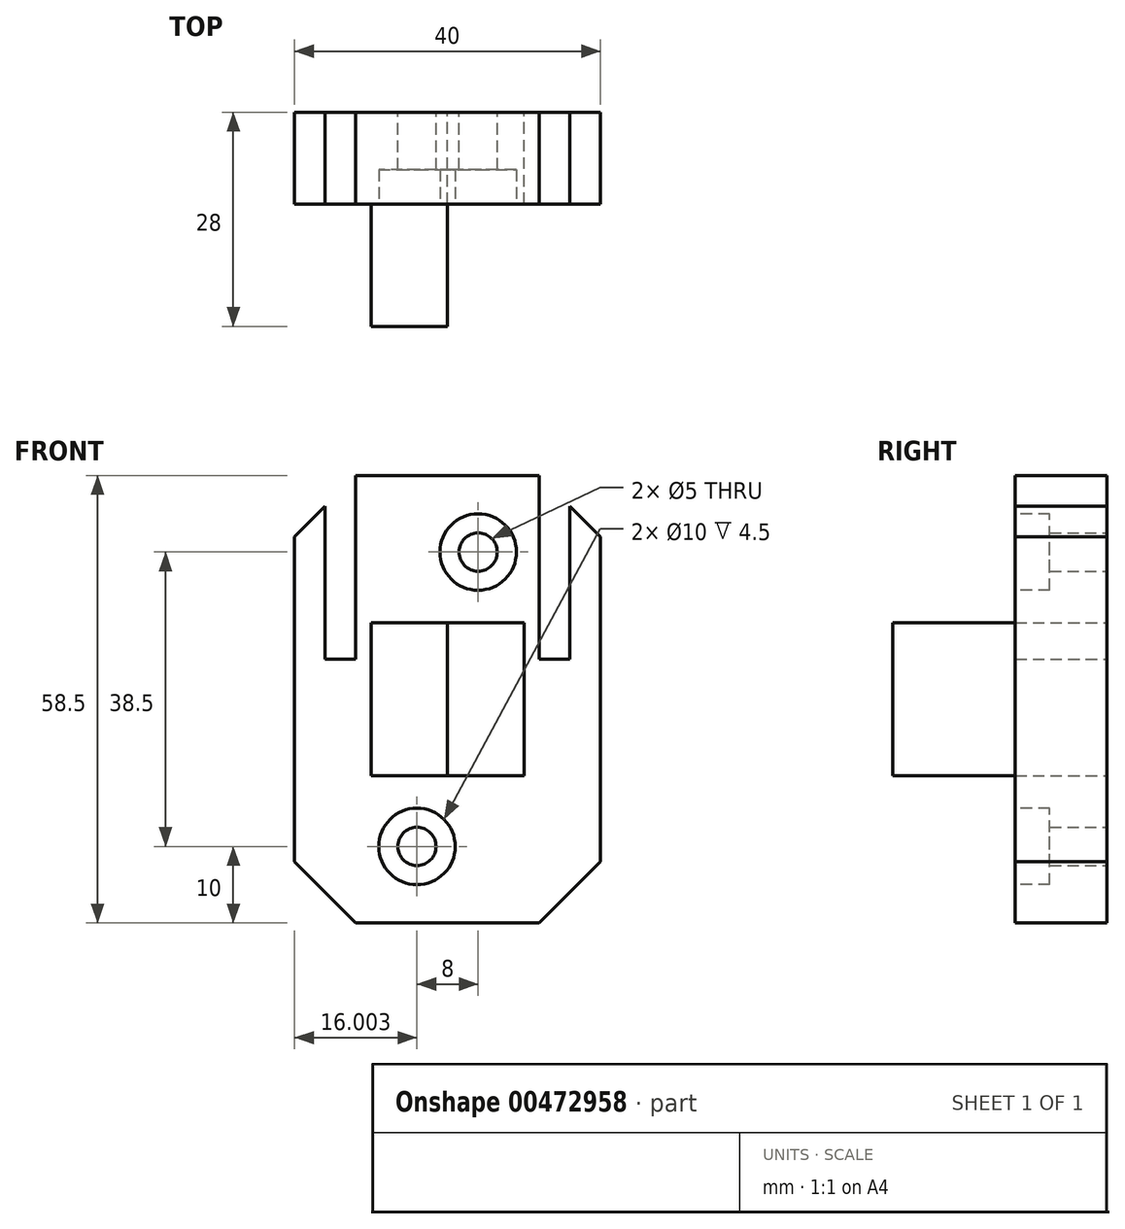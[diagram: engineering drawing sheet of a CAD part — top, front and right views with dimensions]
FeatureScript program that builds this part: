
annotation { "Feature Type Name" : "Feature", "Feature Type Description" : "" }
export const myFeature = defineFeature(function(context is Context, id is Id, definition is map)
    precondition{}
    {
        {
            var Q0;
            Q0=qCreatedBy(makeId("Front.planeOp"),FACE);
            var sketch = newSketch(context, id + "F0", { "sketchPlane" : qUnion([Q0])});
            skLineSegment(sketch, "E0.bottom", {"start": v(10.33, 0) * mm, "end": v(22.33, 0) * mm});
            skLineSegment(sketch, "E0.top", {"start": v(10.33, -58.5) * mm, "end": v(34.33, -58.5) * mm});
            skLineSegment(sketch, "E0.left", {"start": v(2.33, -8) * mm, "end": v(2.33, -50.5) * mm});
            skLineSegment(sketch, "E0.right", {"start": v(42.33, -8) * mm, "end": v(42.33, -50.5) * mm});
            skLineSegment(sketch, "E1", {"start": v(22.33, 0) * mm, "end": v(22.33, -58.5) * mm});
            skLineSegment(sketch, "E2", {"start": v(2.33, -29.25) * mm, "end": v(42.33, -29.25) * mm});
            skCircle(sketch, "E3", {"center": v(18.33, -48.5) * mm, "radius": 2.5 * mm});
            skCircle(sketch, "E4", {"center": v(26.33, -10) * mm, "radius": 2.5 * mm});
            skLineSegment(sketch, "E5", {"start": v(2.33, -8) * mm, "end": v(10.33, 0) * mm});
            skLineSegment(sketch, "E6.MirrorCS", {"start": v(42.33, -8) * mm, "end": v(34.33, 0) * mm});
            skLineSegment(sketch, "E7.MirrorCS", {"start": v(2.33, -50.5) * mm, "end": v(10.33, -58.5) * mm});
            skLineSegment(sketch, "E8.MirrorCS", {"start": v(42.33, -50.5) * mm, "end": v(34.33, -58.5) * mm});
            skPoint(sketch, "E9.orphan", {"position": v(2.33, 0) * mm});
            skPoint(sketch, "E10.orphan", {"position": v(42.33, 0) * mm});
            skPoint(sketch, "E11.orphan", {"position": v(2.33, -58.5) * mm});
            skPoint(sketch, "E12.orphan", {"position": v(42.33, -58.5) * mm});
            skLineSegment(sketch, "E13", {"start": v(22.33, 0) * mm, "end": v(34.33, 0) * mm});
            skLineSegment(sketch, "E14", {"start": v(22.33, -29.25) * mm, "end": v(32.33, -29.25) * mm});
            skLineSegment(sketch, "E15", {"start": v(32.33, -29.25) * mm, "end": v(32.33, -19.25) * mm});
            skLineSegment(sketch, "E16", {"start": v(32.33, -19.25) * mm, "end": v(12.33, -19.25) * mm});
            skLineSegment(sketch, "E17", {"start": v(12.33, -19.25) * mm, "end": v(12.33, -39.25) * mm});
            skLineSegment(sketch, "E18", {"start": v(12.33, -39.25) * mm, "end": v(32.33, -39.25) * mm});
            skLineSegment(sketch, "E19", {"start": v(32.33, -39.25) * mm, "end": v(32.33, -29.25) * mm});
            skSolve(sketch);
        }
        {
            var Q0;
            Q0 = qSketchRegion(id + "F0", true);
            extrude(context, id + "F1", {"entities" : qUnion([Q0]), "depth" : 12 * mm});
        }
        {
            var Q0;
            {var subQ3=sQuery(id+"F0.wireOp",EDGE,"E16");var subQ5=sQuery(id+"F0.wireOp",EDGE,"E17");var subQ7=makeQuery(id+"F0.imprint","INTERSECT",VERTEX,{"derivedFrom":[subQ3,subQ5]});Q0=makeQuery(id+"F0.imprint","IMPRINT",FACE,{"disambiguationData":[TD([[makeQuery(id+"F0.imprint","IMPRINT",EDGE,{"disambiguationData":[TD([[subQ7,1.0]])],"derivedFrom":subQ3}),1.0]])]});}
            var Q1;
            {var subQ0=sQuery(id+"F0.wireOp",EDGE,"E14");Q1=makeQuery(id+"F0.imprint","IMPRINT",FACE,{"disambiguationData":[TD([[makeQuery(id+"F0.imprint","IMPRINT",EDGE,{"derivedFrom":subQ0}),1.0]])]});}
            var Q2;
            {var subQ0=sQuery(id+"F0.wireOp",EDGE,"E14");Q2=makeQuery(id+"F0.imprint","IMPRINT",FACE,{"disambiguationData":[TD([[makeQuery(id+"F0.imprint","IMPRINT",EDGE,{"derivedFrom":subQ0}),-1.0]])]});}
            var Q3;
            {var subQ3=sQuery(id+"F0.wireOp",EDGE,"E18");var subQ5=sQuery(id+"F0.wireOp",EDGE,"E17");var subQ7=makeQuery(id+"F0.imprint","INTERSECT",VERTEX,{"derivedFrom":[subQ5,subQ3]});Q3=makeQuery(id+"F0.imprint","IMPRINT",FACE,{"disambiguationData":[TD([[makeQuery(id+"F0.imprint","IMPRINT",EDGE,{"disambiguationData":[TD([[subQ7,1.0]])],"derivedFrom":subQ5}),1.0]])]});}
            extrude(context, id + "F2", {"entities" : qUnion([Q0, Q1, Q2, Q3]), "operationType" : NewBodyOperationType.ADD, "depth" : 28 * mm});
        }
        {
            var Q0;
            {var subQ0=sQuery(id+"F0.wireOp",EDGE,"E19");var subQ1=sQuery(id+"F0.wireOp",EDGE,"E18");var subQ2=sQuery(id+"F0.wireOp",EDGE,"E17");var subQ3=sQuery(id+"F0.wireOp",EDGE,"E16");var subQ4=sQuery(id+"F0.wireOp",EDGE,"E15");Q0=makeQuery(id+"F2.boolean.opBoolean","MERGE",FACE,{"derivedFrom":[makeQuery(id+"F1.opExtrude","CAP_FACE",FACE,{"disambiguationData":[OSD([sQuery(id+"F0.wireOp",EDGE,"E0.bottom"),sQuery(id+"F0.wireOp",EDGE,"E0.top"),sQuery(id+"F0.wireOp",EDGE,"E0.left"),sQuery(id+"F0.wireOp",EDGE,"E0.right"),sQuery(id+"F0.wireOp",EDGE,"E3"),sQuery(id+"F0.wireOp",EDGE,"E4"),sQuery(id+"F0.wireOp",EDGE,"E5"),sQuery(id+"F0.wireOp",EDGE,"E6.MirrorCS"),sQuery(id+"F0.wireOp",EDGE,"E7.MirrorCS"),sQuery(id+"F0.wireOp",EDGE,"E8.MirrorCS"),sQuery(id+"F0.wireOp",EDGE,"E13"),subQ4,subQ3,subQ2,subQ1,subQ0])],"isStart":true}),makeQuery(id+"F2.opExtrude","CAP_FACE",FACE,{"disambiguationData":[OSD([subQ4,subQ3,subQ2,subQ1,subQ0])],"isStart":true})]});}
            var sketch = newSketch(context, id + "F3", { "sketchPlane" : qUnion([Q0])});
            skLineSegment(sketch, "E20", {"start": v(-42.33, -8) * mm, "end": v(-34.33, -8) * mm});
            skLineSegment(sketch, "E21", {"start": v(-34.33, -8) * mm, "end": v(-34.33, 0) * mm});
            skSolve(sketch);
        }
        {
            var Q0;
            Q0=makeQuery(id+"F3.imprint","IMPRINT",FACE,{"disambiguationData":[TD([[makeQuery(id+"F3.imprint","IMPRINT",EDGE,{"derivedFrom":sQuery(id+"F3.wireOp",EDGE,"E20")}),1.0]])]});
            extrude(context, id + "F4", {"entities" : qUnion([Q0]), "operationType" : NewBodyOperationType.REMOVE, "oppositeDirection" : true, "depth" : 25 * mm});
        }
        {
            var Q0;
            Q0=makeQuery(id+"F4.boolean.opBoolean","COPY",FACE,{"derivedFrom":makeQuery(id+"F4.opExtrude","SWEPT_FACE",FACE,{"disambiguationData":[OSD([sQuery(id+"F3.wireOp",EDGE,"E20")])]})});
            var sketch = newSketch(context, id + "F5", { "sketchPlane" : qUnion([Q0])});
            skLineSegment(sketch, "E22", {"start": v(42.33, -6) * mm, "end": v(34.33, -6) * mm});
            skLineSegment(sketch, "E23", {"start": v(38.33, -12) * mm, "end": v(38.33, 0) * mm});
            skCircle(sketch, "E24", {"center": v(38.33, -6) * mm, "radius": 1.5 * mm});
            skSolve(sketch);
        }
        {
            var Q0;
            {var subQ0=sQuery(id+"F5.wireOp",EDGE,"E23");var subQ1=sQuery(id+"F5.wireOp",EDGE,"E22");var subQ2=makeQuery(id+"F5.imprint","INTERSECT",VERTEX,{"derivedFrom":[subQ1,subQ0]});Q0=makeQuery(id+"F5.imprint","IMPRINT",FACE,{"disambiguationData":[TD([[makeQuery(id+"F5.imprint","IMPRINT",EDGE,{"disambiguationData":[TD([[subQ2,-1.0]])],"derivedFrom":subQ1}),-1.0]])]});}
            var Q1;
            {var subQ0=sQuery(id+"F5.wireOp",EDGE,"E23");var subQ1=sQuery(id+"F5.wireOp",EDGE,"E22");var subQ2=makeQuery(id+"F5.imprint","INTERSECT",VERTEX,{"derivedFrom":[subQ1,subQ0]});Q1=makeQuery(id+"F5.imprint","IMPRINT",FACE,{"disambiguationData":[TD([[makeQuery(id+"F5.imprint","IMPRINT",EDGE,{"disambiguationData":[TD([[subQ2,-1.0]])],"derivedFrom":subQ1}),1.0]])]});}
            var Q2;
            {var subQ0=sQuery(id+"F5.wireOp",EDGE,"E24");var subQ1=sQuery(id+"F5.wireOp",EDGE,"E22");var subQ2=makeQuery(id+"F5.imprint","INTERSECT",VERTEX,{"disambiguationData":[OD(0.0)],"derivedFrom":[subQ1,subQ0]});Q2=makeQuery(id+"F5.imprint","IMPRINT",FACE,{"disambiguationData":[TD([[makeQuery(id+"F5.imprint","IMPRINT",EDGE,{"disambiguationData":[TD([[subQ2,-1.0]])],"derivedFrom":subQ1}),1.0]])]});}
            var Q3;
            {var subQ0=sQuery(id+"F5.wireOp",EDGE,"E24");var subQ1=sQuery(id+"F5.wireOp",EDGE,"E22");var subQ2=makeQuery(id+"F5.imprint","INTERSECT",VERTEX,{"disambiguationData":[OD(0.0)],"derivedFrom":[subQ1,subQ0]});Q3=makeQuery(id+"F5.imprint","IMPRINT",FACE,{"disambiguationData":[TD([[makeQuery(id+"F5.imprint","IMPRINT",EDGE,{"disambiguationData":[TD([[subQ2,-1.0]])],"derivedFrom":subQ1}),-1.0]])]});}
            extrude(context, id + "F6", {"entities" : qUnion([Q0, Q1, Q2, Q3]), "operationType" : NewBodyOperationType.REMOVE, "oppositeDirection" : true, "depth" : 16 * mm});
        }
        {
            var Q0;
            {var subQ0=sQuery(id+"F0.wireOp",EDGE,"E19");var subQ1=sQuery(id+"F0.wireOp",EDGE,"E18");var subQ2=sQuery(id+"F0.wireOp",EDGE,"E17");var subQ3=sQuery(id+"F0.wireOp",EDGE,"E16");var subQ4=sQuery(id+"F0.wireOp",EDGE,"E15");Q0=makeQuery(id+"F2.boolean.opBoolean","MERGE",FACE,{"derivedFrom":[makeQuery(id+"F1.opExtrude","CAP_FACE",FACE,{"disambiguationData":[OSD([sQuery(id+"F0.wireOp",EDGE,"E0.bottom"),sQuery(id+"F0.wireOp",EDGE,"E0.top"),sQuery(id+"F0.wireOp",EDGE,"E0.left"),sQuery(id+"F0.wireOp",EDGE,"E0.right"),sQuery(id+"F0.wireOp",EDGE,"E3"),sQuery(id+"F0.wireOp",EDGE,"E4"),sQuery(id+"F0.wireOp",EDGE,"E5"),sQuery(id+"F0.wireOp",EDGE,"E6.MirrorCS"),sQuery(id+"F0.wireOp",EDGE,"E7.MirrorCS"),sQuery(id+"F0.wireOp",EDGE,"E8.MirrorCS"),sQuery(id+"F0.wireOp",EDGE,"E13"),subQ4,subQ3,subQ2,subQ1,subQ0])],"isStart":true}),makeQuery(id+"F2.opExtrude","CAP_FACE",FACE,{"disambiguationData":[OSD([subQ4,subQ3,subQ2,subQ1,subQ0])],"isStart":true})]});}
            var sketch = newSketch(context, id + "F7", { "sketchPlane" : qUnion([Q0])});
            skLineSegment(sketch, "E25", {"start": v(-38.33, -8) * mm, "end": v(-38.33, 0) * mm});
            skLineSegment(sketch, "E26", {"start": v(-22.33, 0) * mm, "end": v(-22.33, -14.44) * mm});
            skPoint(sketch, "E26.endSnap0", {"position": v(-22.33, 0) * mm});
            skLineSegment(sketch, "E27.MirrorCS", {"start": v(-6.33, -8) * mm, "end": v(-6.33, 0) * mm});
            skLineSegment(sketch, "E28", {"start": v(-2.33, -8) * mm, "end": v(-10.33, -8) * mm});
            skLineSegment(sketch, "E29", {"start": v(-10.33, -8) * mm, "end": v(-10.33, 0) * mm});
            skSolve(sketch);
        }
        {
            var Q0;
            {var subQ5=sQuery(id+"F7.wireOp",EDGE,"E29");Q0=makeQuery(id+"F7.imprint","IMPRINT",FACE,{"disambiguationData":[TD([[makeQuery(id+"F7.imprint","IMPRINT",EDGE,{"derivedFrom":subQ5}),-1.0]])]});}
            var Q1;
            {var subQ0=sQuery(id+"F7.wireOp",EDGE,"E28");var subQ1=sQuery(id+"F7.wireOp",EDGE,"E27.MirrorCS");var subQ2=makeQuery(id+"F7.imprint","INTERSECT",VERTEX,{"derivedFrom":[subQ1,subQ0]});Q1=makeQuery(id+"F7.imprint","IMPRINT",FACE,{"disambiguationData":[TD([[makeQuery(id+"F7.imprint","IMPRINT",EDGE,{"disambiguationData":[TD([[subQ2,-1.0]])],"derivedFrom":subQ1}),-1.0]])]});}
            extrude(context, id + "F8", {"entities" : qUnion([Q0, Q1]), "operationType" : NewBodyOperationType.REMOVE, "oppositeDirection" : true, "depth" : 25 * mm});
        }
        {
            var Q0;
            Q0=makeQuery(id+"F8.boolean.opBoolean","COPY",FACE,{"derivedFrom":makeQuery(id+"F8.opExtrude","SWEPT_FACE",FACE,{"disambiguationData":[OSD([sQuery(id+"F7.wireOp",EDGE,"E28")])]})});
            var sketch = newSketch(context, id + "F9", { "sketchPlane" : qUnion([Q0])});
            skLineSegment(sketch, "E30", {"start": v(2.33, -6) * mm, "end": v(10.33, -6) * mm});
            skLineSegment(sketch, "E31", {"start": v(6.33, -12) * mm, "end": v(6.33, 0) * mm});
            skCircle(sketch, "E32", {"center": v(6.33, -6) * mm, "radius": 1.5 * mm});
            skSolve(sketch);
        }
        {
            var Q0;
            {var subQ0=sQuery(id+"F9.wireOp",EDGE,"E32");var subQ1=sQuery(id+"F9.wireOp",EDGE,"E30");var subQ2=makeQuery(id+"F9.imprint","INTERSECT",VERTEX,{"disambiguationData":[OD(0.0)],"derivedFrom":[subQ1,subQ0]});Q0=makeQuery(id+"F9.imprint","IMPRINT",FACE,{"disambiguationData":[TD([[makeQuery(id+"F9.imprint","IMPRINT",EDGE,{"disambiguationData":[TD([[subQ2,-1.0]])],"derivedFrom":subQ1}),-1.0]])]});}
            var Q1;
            {var subQ0=sQuery(id+"F9.wireOp",EDGE,"E32");var subQ1=sQuery(id+"F9.wireOp",EDGE,"E30");var subQ2=makeQuery(id+"F9.imprint","INTERSECT",VERTEX,{"disambiguationData":[OD(0.0)],"derivedFrom":[subQ1,subQ0]});Q1=makeQuery(id+"F9.imprint","IMPRINT",FACE,{"disambiguationData":[TD([[makeQuery(id+"F9.imprint","IMPRINT",EDGE,{"disambiguationData":[TD([[subQ2,-1.0]])],"derivedFrom":subQ1}),1.0]])]});}
            var Q2;
            {var subQ0=sQuery(id+"F9.wireOp",EDGE,"E31");var subQ1=sQuery(id+"F9.wireOp",EDGE,"E30");var subQ2=makeQuery(id+"F9.imprint","INTERSECT",VERTEX,{"derivedFrom":[subQ1,subQ0]});Q2=makeQuery(id+"F9.imprint","IMPRINT",FACE,{"disambiguationData":[TD([[makeQuery(id+"F9.imprint","IMPRINT",EDGE,{"disambiguationData":[TD([[subQ2,-1.0]])],"derivedFrom":subQ1}),1.0]])]});}
            var Q3;
            {var subQ0=sQuery(id+"F9.wireOp",EDGE,"E31");var subQ1=sQuery(id+"F9.wireOp",EDGE,"E30");var subQ2=makeQuery(id+"F9.imprint","INTERSECT",VERTEX,{"derivedFrom":[subQ1,subQ0]});Q3=makeQuery(id+"F9.imprint","IMPRINT",FACE,{"disambiguationData":[TD([[makeQuery(id+"F9.imprint","IMPRINT",EDGE,{"disambiguationData":[TD([[subQ2,-1.0]])],"derivedFrom":subQ1}),-1.0]])]});}
            extrude(context, id + "F10", {"entities" : qUnion([Q0, Q1, Q2, Q3]), "operationType" : NewBodyOperationType.REMOVE, "oppositeDirection" : true, "depth" : 16 * mm});
        }
        {
            var Q0;
            Q0=makeQuery(id+"F8.boolean.opBoolean","COPY",FACE,{"derivedFrom":makeQuery(id+"F8.opExtrude","SWEPT_FACE",FACE,{"disambiguationData":[OSD([sQuery(id+"F7.wireOp",EDGE,"E28")])]})});
            extrude(context, id + "F11", {"entities" : qUnion([Q0]), "operationType" : NewBodyOperationType.ADD, "depth" : 25 * mm});
        }
        {
            var Q0;
            {var subQ0=sQuery(id+"F0.wireOp",EDGE,"E19");var subQ1=sQuery(id+"F0.wireOp",EDGE,"E18");var subQ2=sQuery(id+"F0.wireOp",EDGE,"E17");var subQ3=sQuery(id+"F0.wireOp",EDGE,"E16");var subQ4=sQuery(id+"F0.wireOp",EDGE,"E15");var subQ5=sQuery(id+"F0.wireOp",EDGE,"E13");var subQ6=sQuery(id+"F0.wireOp",EDGE,"E8.MirrorCS");var subQ7=sQuery(id+"F0.wireOp",EDGE,"E7.MirrorCS");var subQ8=sQuery(id+"F0.wireOp",EDGE,"E6.MirrorCS");var subQ9=sQuery(id+"F0.wireOp",EDGE,"E5");var subQ10=sQuery(id+"F0.wireOp",EDGE,"E4");var subQ11=sQuery(id+"F0.wireOp",EDGE,"E3");var subQ12=sQuery(id+"F0.wireOp",EDGE,"E0.right");var subQ13=sQuery(id+"F0.wireOp",EDGE,"E0.left");var subQ14=sQuery(id+"F0.wireOp",EDGE,"E0.top");var subQ15=sQuery(id+"F0.wireOp",EDGE,"E0.bottom");Q0=makeQuery(id+"F11.boolean.opBoolean","MERGE",FACE,{"derivedFrom":[makeQuery(id+"F1.opExtrude","CAP_FACE",FACE,{"disambiguationData":[OSD([subQ15,subQ14,subQ13,subQ12,subQ11,subQ10,subQ9,subQ8,subQ7,subQ6,subQ5,subQ4,subQ3,subQ2,subQ1,subQ0])],"isStart":false}),makeQuery(id+"F11.opExtrude","SWEPT_FACE",FACE,{"disambiguationData":[OSD([subQ15,subQ14,subQ13,subQ12,subQ11,subQ10,subQ9,subQ8,subQ7,subQ6,subQ5,subQ4,subQ3,subQ2,subQ1,subQ0,sQuery(id+"F7.wireOp",EDGE,"E28")])]})]});}
            var sketch = newSketch(context, id + "F12", { "sketchPlane" : qUnion([Q0])});
            skLineSegment(sketch, "E33", {"start": v(10.33, 0) * mm, "end": v(10.33, -8) * mm});
            skLineSegment(sketch, "E34", {"start": v(10.33, -8) * mm, "end": v(2.33, -8) * mm});
            skLineSegment(sketch, "E35", {"start": v(2.33, -8) * mm, "end": v(10.33, 0) * mm});
            skSolve(sketch);
        }
        {
            var Q0;
            {var subQ0=sQuery(id+"F12.wireOp",EDGE,"E35");Q0=makeQuery(id+"F12.imprint","IMPRINT",FACE,{"disambiguationData":[TD([[makeQuery(id+"F12.imprint","IMPRINT",EDGE,{"derivedFrom":subQ0}),1.0]])]});}
            extrude(context, id + "F13", {"entities" : qUnion([Q0]), "operationType" : NewBodyOperationType.REMOVE, "oppositeDirection" : true, "depth" : 25 * mm});
        }
        {
            var Q0;
            Q0=makeQuery(id+"F4.boolean.opBoolean","COPY",FACE,{"derivedFrom":makeQuery(id+"F4.opExtrude","SWEPT_FACE",FACE,{"disambiguationData":[OSD([sQuery(id+"F3.wireOp",EDGE,"E20")])]})});
            extrude(context, id + "F14", {"entities" : qUnion([Q0]), "operationType" : NewBodyOperationType.ADD, "depth" : 25 * mm});
        }
        {
            var Q0;
            {var subQ0=sQuery(id+"F0.wireOp",EDGE,"E19");var subQ1=sQuery(id+"F0.wireOp",EDGE,"E18");var subQ2=sQuery(id+"F0.wireOp",EDGE,"E17");var subQ3=sQuery(id+"F0.wireOp",EDGE,"E16");var subQ4=sQuery(id+"F0.wireOp",EDGE,"E15");var subQ5=sQuery(id+"F0.wireOp",EDGE,"E13");var subQ6=sQuery(id+"F0.wireOp",EDGE,"E8.MirrorCS");var subQ7=sQuery(id+"F0.wireOp",EDGE,"E7.MirrorCS");var subQ8=sQuery(id+"F0.wireOp",EDGE,"E6.MirrorCS");var subQ9=sQuery(id+"F0.wireOp",EDGE,"E5");var subQ10=sQuery(id+"F0.wireOp",EDGE,"E4");var subQ11=sQuery(id+"F0.wireOp",EDGE,"E3");var subQ12=sQuery(id+"F0.wireOp",EDGE,"E0.right");var subQ13=sQuery(id+"F0.wireOp",EDGE,"E0.left");var subQ14=sQuery(id+"F0.wireOp",EDGE,"E0.top");var subQ15=sQuery(id+"F0.wireOp",EDGE,"E0.bottom");Q0=makeQuery(id+"F14.boolean.opBoolean","MERGE",FACE,{"derivedFrom":[makeQuery(id+"F11.boolean.opBoolean","MERGE",FACE,{"derivedFrom":[makeQuery(id+"F1.opExtrude","CAP_FACE",FACE,{"disambiguationData":[OSD([subQ15,subQ14,subQ13,subQ12,subQ11,subQ10,subQ9,subQ8,subQ7,subQ6,subQ5,subQ4,subQ3,subQ2,subQ1,subQ0])],"isStart":false}),makeQuery(id+"F11.opExtrude","SWEPT_FACE",FACE,{"disambiguationData":[OSD([subQ15,subQ14,subQ13,subQ12,subQ11,subQ10,subQ9,subQ8,subQ7,subQ6,subQ5,subQ4,subQ3,subQ2,subQ1,subQ0,sQuery(id+"F7.wireOp",EDGE,"E28")])]})]}),makeQuery(id+"F14.opExtrude","SWEPT_FACE",FACE,{"disambiguationData":[OSD([subQ15,subQ14,subQ13,subQ12,subQ11,subQ10,subQ9,subQ8,subQ7,subQ6,subQ5,subQ4,subQ3,subQ2,subQ1,subQ0,sQuery(id+"F3.wireOp",EDGE,"E20")])]})]});}
            var sketch = newSketch(context, id + "F15", { "sketchPlane" : qUnion([Q0])});
            skLineSegment(sketch, "E36", {"start": v(34.33, 0) * mm, "end": v(34.33, -8) * mm});
            skLineSegment(sketch, "E37", {"start": v(34.33, -8) * mm, "end": v(42.33, -8) * mm});
            skLineSegment(sketch, "E38", {"start": v(42.33, -8) * mm, "end": v(34.33, 0) * mm});
            skSolve(sketch);
        }
        {
            var Q0;
            {var subQ0=sQuery(id+"F15.wireOp",EDGE,"E38");Q0=makeQuery(id+"F15.imprint","IMPRINT",FACE,{"disambiguationData":[TD([[makeQuery(id+"F15.imprint","IMPRINT",EDGE,{"derivedFrom":subQ0}),-1.0]])]});}
            extrude(context, id + "F16", {"entities" : qUnion([Q0]), "operationType" : NewBodyOperationType.REMOVE, "oppositeDirection" : true, "depth" : 25 * mm});
        }
        {
            var Q0;
            Q0=makeQuery(id+"F2.opExtrude","SWEPT_FACE",FACE,{"disambiguationData":[OSD([sQuery(id+"F0.wireOp",EDGE,"E16")])]});
            var sketch = newSketch(context, id + "F17", { "sketchPlane" : qUnion([Q0])});
            skLineSegment(sketch, "E39", {"start": v(12.33, -20) * mm, "end": v(32.33, -20) * mm});
            skLineSegment(sketch, "E40", {"start": v(22.33, -12) * mm, "end": v(22.33, -28) * mm});
            skCircle(sketch, "E41", {"center": v(22.33, -20) * mm, "radius": 4 * mm});
            skSolve(sketch);
        }
        {
            var Q0;
            {var subQ0=sQuery(id+"F17.wireOp",EDGE,"E41");var subQ1=sQuery(id+"F17.wireOp",EDGE,"E39");var subQ2=makeQuery(id+"F17.imprint","INTERSECT",VERTEX,{"disambiguationData":[OD(0.0)],"derivedFrom":[subQ1,subQ0]});Q0=makeQuery(id+"F17.imprint","IMPRINT",FACE,{"disambiguationData":[TD([[makeQuery(id+"F17.imprint","IMPRINT",EDGE,{"disambiguationData":[TD([[subQ2,-1.0]])],"derivedFrom":subQ1}),-1.0]])]});}
            var Q1;
            {var subQ0=sQuery(id+"F17.wireOp",EDGE,"E41");var subQ1=sQuery(id+"F17.wireOp",EDGE,"E39");var subQ2=makeQuery(id+"F17.imprint","INTERSECT",VERTEX,{"disambiguationData":[OD(0.0)],"derivedFrom":[subQ1,subQ0]});Q1=makeQuery(id+"F17.imprint","IMPRINT",FACE,{"disambiguationData":[TD([[makeQuery(id+"F17.imprint","IMPRINT",EDGE,{"disambiguationData":[TD([[subQ2,-1.0]])],"derivedFrom":subQ1}),1.0]])]});}
            var Q2;
            {var subQ0=sQuery(id+"F17.wireOp",EDGE,"E40");var subQ1=sQuery(id+"F17.wireOp",EDGE,"E39");var subQ2=makeQuery(id+"F17.imprint","INTERSECT",VERTEX,{"derivedFrom":[subQ1,subQ0]});Q2=makeQuery(id+"F17.imprint","IMPRINT",FACE,{"disambiguationData":[TD([[makeQuery(id+"F17.imprint","IMPRINT",EDGE,{"disambiguationData":[TD([[subQ2,-1.0]])],"derivedFrom":subQ1}),1.0]])]});}
            var Q3;
            {var subQ0=sQuery(id+"F17.wireOp",EDGE,"E40");var subQ1=sQuery(id+"F17.wireOp",EDGE,"E39");var subQ2=makeQuery(id+"F17.imprint","INTERSECT",VERTEX,{"derivedFrom":[subQ1,subQ0]});Q3=makeQuery(id+"F17.imprint","IMPRINT",FACE,{"disambiguationData":[TD([[makeQuery(id+"F17.imprint","IMPRINT",EDGE,{"disambiguationData":[TD([[subQ2,-1.0]])],"derivedFrom":subQ1}),-1.0]])]});}
            extrude(context, id + "F18", {"entities" : qUnion([Q0, Q1, Q2, Q3]), "operationType" : NewBodyOperationType.REMOVE, "oppositeDirection" : true, "depth" : 25 * mm});
        }
        {
            var Q0;
            {var subQ0=sQuery(id+"F0.wireOp",EDGE,"E19");var subQ1=sQuery(id+"F0.wireOp",EDGE,"E18");var subQ2=sQuery(id+"F0.wireOp",EDGE,"E17");var subQ3=sQuery(id+"F0.wireOp",EDGE,"E16");var subQ4=sQuery(id+"F0.wireOp",EDGE,"E15");var subQ5=sQuery(id+"F0.wireOp",EDGE,"E13");var subQ6=sQuery(id+"F0.wireOp",EDGE,"E8.MirrorCS");var subQ7=sQuery(id+"F0.wireOp",EDGE,"E7.MirrorCS");var subQ8=sQuery(id+"F0.wireOp",EDGE,"E6.MirrorCS");var subQ9=sQuery(id+"F0.wireOp",EDGE,"E5");var subQ10=sQuery(id+"F0.wireOp",EDGE,"E4");var subQ11=sQuery(id+"F0.wireOp",EDGE,"E3");var subQ12=sQuery(id+"F0.wireOp",EDGE,"E0.right");var subQ13=sQuery(id+"F0.wireOp",EDGE,"E0.left");var subQ14=sQuery(id+"F0.wireOp",EDGE,"E0.top");var subQ15=sQuery(id+"F0.wireOp",EDGE,"E0.bottom");Q0=makeQuery(id+"F14.boolean.opBoolean","MERGE",FACE,{"derivedFrom":[makeQuery(id+"F11.boolean.opBoolean","MERGE",FACE,{"derivedFrom":[makeQuery(id+"F1.opExtrude","CAP_FACE",FACE,{"disambiguationData":[OSD([subQ15,subQ14,subQ13,subQ12,subQ11,subQ10,subQ9,subQ8,subQ7,subQ6,subQ5,subQ4,subQ3,subQ2,subQ1,subQ0])],"isStart":false}),makeQuery(id+"F11.opExtrude","SWEPT_FACE",FACE,{"disambiguationData":[OSD([subQ15,subQ14,subQ13,subQ12,subQ11,subQ10,subQ9,subQ8,subQ7,subQ6,subQ5,subQ4,subQ3,subQ2,subQ1,subQ0,sQuery(id+"F7.wireOp",EDGE,"E28")])]})]}),makeQuery(id+"F14.opExtrude","SWEPT_FACE",FACE,{"disambiguationData":[OSD([subQ15,subQ14,subQ13,subQ12,subQ11,subQ10,subQ9,subQ8,subQ7,subQ6,subQ5,subQ4,subQ3,subQ2,subQ1,subQ0,sQuery(id+"F3.wireOp",EDGE,"E20")])]})]});}
            var sketch = newSketch(context, id + "F19", { "sketchPlane" : qUnion([Q0])});
            skCircle(sketch, "E42", {"center": v(26.33, -10) * mm, "radius": 5 * mm});
            skCircle(sketch, "E43", {"center": v(18.33, -48.5) * mm, "radius": 5 * mm});
            skSolve(sketch);
        }
        {
            var Q0;
            Q0=makeQuery(id+"F19.imprint","IMPRINT",FACE,{"disambiguationData":[TD([[makeQuery(id+"F19.imprint","IMPRINT",EDGE,{"derivedFrom":sQuery(id+"F19.wireOp",EDGE,"E42")}),1.0]])]});
            extrude(context, id + "F20", {"entities" : qUnion([Q0]), "operationType" : NewBodyOperationType.REMOVE, "oppositeDirection" : true, "depth" : 4.5 * mm});
        }
        {
            var Q0;
            Q0=makeQuery(id+"F19.imprint","IMPRINT",FACE,{"disambiguationData":[TD([[makeQuery(id+"F19.imprint","IMPRINT",EDGE,{"derivedFrom":sQuery(id+"F19.wireOp",EDGE,"E43")}),1.0]])]});
            extrude(context, id + "F21", {"entities" : qUnion([Q0]), "operationType" : NewBodyOperationType.REMOVE, "oppositeDirection" : true, "depth" : 4.5 * mm});
        }
    });
